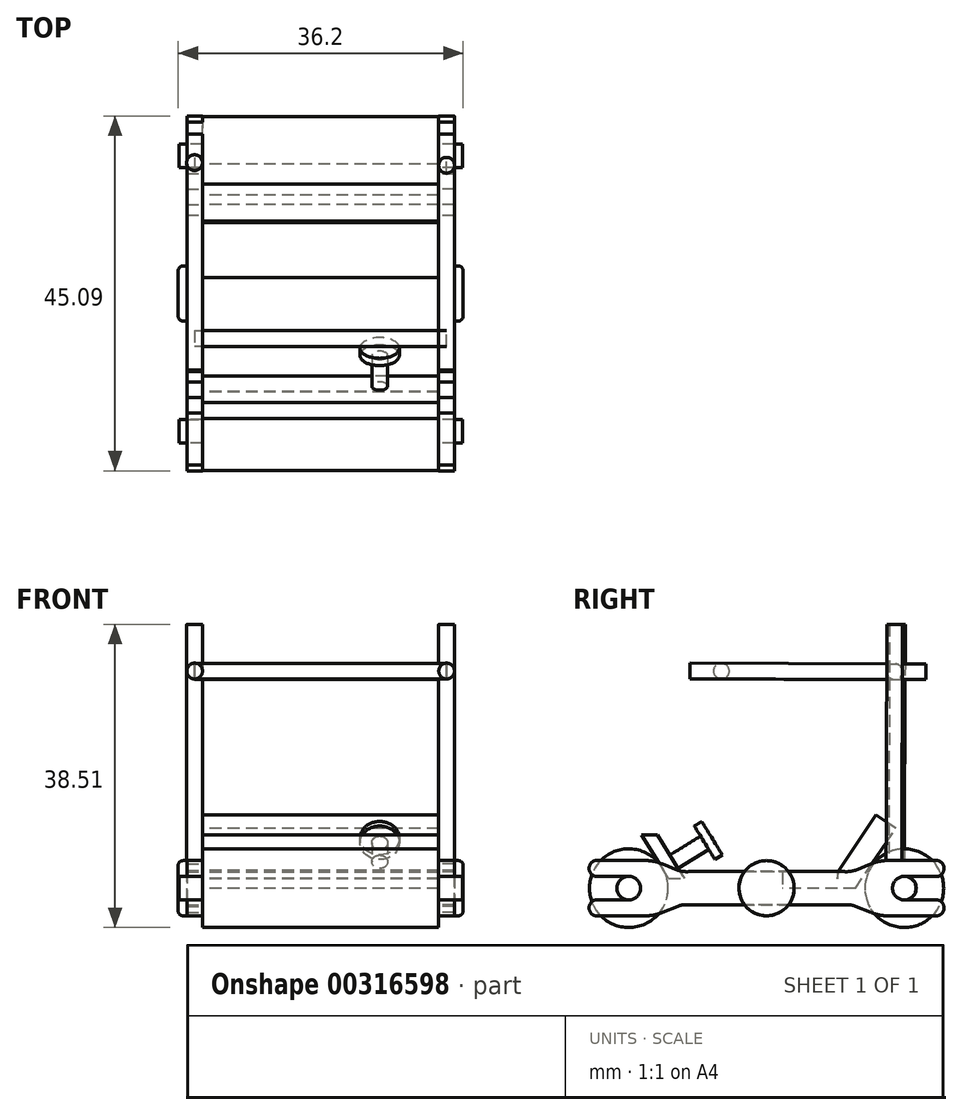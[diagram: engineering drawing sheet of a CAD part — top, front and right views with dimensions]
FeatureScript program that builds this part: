
annotation { "Feature Type Name" : "Feature", "Feature Type Description" : "" }
export const myFeature = defineFeature(function(context is Context, id is Id, definition is map)
    precondition{}
    {
        {
            var Q0;
            Q0=qCreatedBy(makeId("Right.planeOp"),FACE);
            var sketch = newSketch(context, id + "F0", { "sketchPlane" : qUnion([Q0])});
            skCircle(sketch, "E0", {"center": v(0, 0) * mm, "radius": 5 * mm});
            skCircle(sketch, "E1", {"center": v(-35, 0) * mm, "radius": 5 * mm});
            skSolve(sketch);
        }
        {
            var Q0;
            Q0 = qSketchRegion(id + "F0", true);
            extrude(context, id + "F1", {"entities" : qUnion([Q0]), "depth" : 30 * mm});
        }
        {
            var Q0;
            Q0=makeQuery(id+"F1.opExtrude","CAP_FACE",FACE,{"disambiguationData":[OSD([sQuery(id+"F0.wireOp",EDGE,"E0")])],"isStart":false});
            var sketch = newSketch(context, id + "F2", { "sketchPlane" : qUnion([Q0])});
            skCircle(sketch, "E2", {"center": v(0, 0) * mm, "radius": 1.5 * mm});
            skCircle(sketch, "E3", {"center": v(-35, 0) * mm, "radius": 1.5 * mm});
            skSolve(sketch);
        }
        {
            var Q0;
            Q0 = qSketchRegion(id + "F2", true);
            extrude(context, id + "F3", {"entities" : qUnion([Q0]), "operationType" : NewBodyOperationType.ADD, "depth" : 3 * mm, "hasSecondDirection" : true, "secondDirectionOppositeDirection" : true, "secondDirectionDepth" : 33 * mm});
        }
        {
            var Q0;
            Q0=makeQuery(id+"F1.opExtrude","CAP_FACE",FACE,{"disambiguationData":[OSD([sQuery(id+"F0.wireOp",EDGE,"E0")])],"isStart":false});
            var sketch = newSketch(context, id + "F4", { "sketchPlane" : qUnion([Q0])});
            skLineSegment(sketch, "E4", {"start": v(-35, 3.5) * mm, "end": v(-39.28, 3.5) * mm});
            skPoint(sketch, "E5.orphan", {"position": v(-45, -3.5) * mm});
            skLineSegment(sketch, "E6", {"start": v(-35, 1.5) * mm, "end": v(-39.28, 1.5) * mm});
            skArc(sketch, "E7", {"start": v(-33.5, 0) * mm, "mid": v(-33.94, 1.06) * mm, "end": v(-35, 1.5) * mm});
            skLineSegment(sketch, "E8", {"start": v(-30.73, 3.07) * mm, "end": v(-28.77, 2.29) * mm});
            skArc(sketch, "E9", {"start": v(-30.73, 3.07) * mm, "mid": v(-31.7, 3.38) * mm, "end": v(-32.7, 3.5) * mm});
            skLineSegment(sketch, "E10.trimOffspring", {"start": v(-32.7, 3.5) * mm, "end": v(-35, 3.5) * mm});
            skArc(sketch, "E11", {"start": v(-39.28, 3.5) * mm, "mid": v(-40.04, 2.5) * mm, "end": v(-39.28, 1.5) * mm});
            skPoint(sketch, "E12.start.orphan", {"position": v(-40, 2.5) * mm});
            skPoint(sketch, "E13.orphan", {"position": v(-40, 3.5) * mm});
            skPoint(sketch, "E14.orphan", {"position": v(-40, 1.5) * mm});
            skLineSegment(sketch, "E15", {"start": v(5, 11.22) * mm, "end": v(-17.5, 11.22) * mm, "construction": true});
            skLineSegment(sketch, "E16", {"start": v(-17.5, 11.22) * mm, "end": v(-17.5, -11.24) * mm, "construction": true});
            skArc(sketch, "E17", {"start": v(-28.77, 2.29) * mm, "mid": v(-28.1, 2.13) * mm, "end": v(-27.42, 2.1) * mm});
            skPoint(sketch, "E18.orphan", {"position": v(-28.31, 2.1) * mm});
            skLineSegment(sketch, "E19.trimOffspring", {"start": v(-27.42, 2.1) * mm, "end": v(-17.5, 2.1) * mm});
            skLineSegment(sketch, "E20", {"start": v(-53.45, 0) * mm, "end": v(6.7, 0) * mm, "construction": true});
            skLineSegment(sketch, "E21.MirrorCS", {"start": v(-7.58, 2.1) * mm, "end": v(-17.5, 2.1) * mm});
            skArc(sketch, "E22.MirrorCS", {"start": v(4.28, 3.5) * mm, "mid": v(5.04, 2.5) * mm, "end": v(4.28, 1.5) * mm});
            skArc(sketch, "E23.MirrorCS", {"start": v(-6.23, 2.29) * mm, "mid": v(-6.9, 2.13) * mm, "end": v(-7.58, 2.1) * mm});
            skLineSegment(sketch, "E24.MirrorCS", {"start": v(0, 3.5) * mm, "end": v(4.28, 3.5) * mm});
            skPoint(sketch, "E25.MirrorP", {"position": v(-6.69, 2.1) * mm});
            skLineSegment(sketch, "E26.MirrorCS", {"start": v(0, 1.5) * mm, "end": v(4.28, 1.5) * mm});
            skArc(sketch, "E27.MirrorCS", {"start": v(-1.5, 0) * mm, "mid": v(-1.06, 1.06) * mm, "end": v(0, 1.5) * mm});
            skPoint(sketch, "E28.MirrorP", {"position": v(5, 1.5) * mm});
            skLineSegment(sketch, "E29.MirrorCS", {"start": v(-2.3, 3.5) * mm, "end": v(0, 3.5) * mm});
            skLineSegment(sketch, "E30.MirrorCS", {"start": v(-4.27, 3.07) * mm, "end": v(-6.23, 2.29) * mm});
            skArc(sketch, "E31.MirrorCS", {"start": v(-4.27, 3.07) * mm, "mid": v(-3.3, 3.38) * mm, "end": v(-2.3, 3.5) * mm});
            skPoint(sketch, "E32.MirrorP", {"position": v(5, 2.5) * mm});
            skPoint(sketch, "E33.MirrorP", {"position": v(5, 3.5) * mm});
            skArc(sketch, "E34.MirrorCS", {"start": v(-6.23, -2.29) * mm, "mid": v(-6.9, -2.13) * mm, "end": v(-7.58, -2.1) * mm});
            skArc(sketch, "E35.MirrorCS", {"start": v(-4.27, -3.07) * mm, "mid": v(-3.3, -3.38) * mm, "end": v(-2.3, -3.5) * mm});
            skLineSegment(sketch, "E36.MirrorCS", {"start": v(-4.27, -3.07) * mm, "end": v(-6.23, -2.29) * mm});
            skLineSegment(sketch, "E37.MirrorCS", {"start": v(-2.3, -3.5) * mm, "end": v(0, -3.5) * mm});
            skLineSegment(sketch, "E38.MirrorCS", {"start": v(-30.73, -3.07) * mm, "end": v(-28.77, -2.29) * mm});
            skArc(sketch, "E39.MirrorCS", {"start": v(4.28, -3.5) * mm, "mid": v(5.04, -2.5) * mm, "end": v(4.28, -1.5) * mm});
            skArc(sketch, "E40.MirrorCS", {"start": v(-30.73, -3.07) * mm, "mid": v(-31.7, -3.38) * mm, "end": v(-32.7, -3.5) * mm});
            skArc(sketch, "E41.MirrorCS", {"start": v(-39.28, -3.5) * mm, "mid": v(-40.04, -2.5) * mm, "end": v(-39.28, -1.5) * mm});
            skLineSegment(sketch, "E42.MirrorCS", {"start": v(-32.7, -3.5) * mm, "end": v(-35, -3.5) * mm});
            skArc(sketch, "E43.MirrorCS", {"start": v(-28.77, -2.29) * mm, "mid": v(-28.1, -2.13) * mm, "end": v(-27.42, -2.1) * mm});
            skArc(sketch, "E44.MirrorCS", {"start": v(-1.5, 0) * mm, "mid": v(-1.06, -1.06) * mm, "end": v(0, -1.5) * mm});
            skArc(sketch, "E45.MirrorCS", {"start": v(-33.5, 0) * mm, "mid": v(-33.94, -1.06) * mm, "end": v(-35, -1.5) * mm});
            skLineSegment(sketch, "E46.MirrorCS", {"start": v(-7.58, -2.1) * mm, "end": v(-17.5, -2.1) * mm});
            skLineSegment(sketch, "E47.MirrorCS", {"start": v(0, -3.5) * mm, "end": v(4.28, -3.5) * mm});
            skLineSegment(sketch, "E48.MirrorCS", {"start": v(-35, -3.5) * mm, "end": v(-39.28, -3.5) * mm});
            skPoint(sketch, "E49.MirrorP", {"position": v(5, -3.5) * mm});
            skLineSegment(sketch, "E50.MirrorCS", {"start": v(0, -1.5) * mm, "end": v(4.28, -1.5) * mm});
            skPoint(sketch, "E51.MirrorP", {"position": v(-45, 3.5) * mm});
            skPoint(sketch, "E52.MirrorP", {"position": v(5, -1.5) * mm});
            skPoint(sketch, "E53.MirrorP", {"position": v(-40, -3.5) * mm});
            skPoint(sketch, "E54.MirrorP", {"position": v(5, -2.5) * mm});
            skPoint(sketch, "E55.MirrorP", {"position": v(-28.31, -2.1) * mm});
            skPoint(sketch, "E56.MirrorP", {"position": v(-40, -1.5) * mm});
            skLineSegment(sketch, "E57.MirrorCS", {"start": v(-35, -1.5) * mm, "end": v(-39.28, -1.5) * mm});
            skPoint(sketch, "E58.MirrorP", {"position": v(-6.69, -2.1) * mm});
            skPoint(sketch, "E59.MirrorP", {"position": v(-40, -2.5) * mm});
            skLineSegment(sketch, "E60.MirrorCS", {"start": v(-27.42, -2.1) * mm, "end": v(-17.5, -2.1) * mm});
            skSolve(sketch);
        }
        {
            var Q0;
            Q0 = qSketchRegion(id + "F4", true);
            extrude(context, id + "F5", {"entities" : qUnion([Q0]), "depth" : 2 * mm});
        }
        {
            var Q0;
            Q0=makeQuery(id+"F1.opExtrude","CAP_FACE",FACE,{"disambiguationData":[OSD([sQuery(id+"F0.wireOp",EDGE,"E0")])],"isStart":true});
            var sketch = newSketch(context, id + "F6", { "sketchPlane" : qUnion([Q0])});
            skPoint(sketch, "E61.orphan", {"position": v(6.62, -3.1) * mm});
            skLineSegment(sketch, "E62", {"start": v(-0.01, 3.5) * mm, "end": v(-4.3, 3.5) * mm});
            skPoint(sketch, "E63.orphan", {"position": v(-26.63, -3.7) * mm});
            skLineSegment(sketch, "E64", {"start": v(-0.01, 1.5) * mm, "end": v(-4.3, 1.5) * mm});
            skArc(sketch, "E65", {"start": v(1.49, 0) * mm, "mid": v(1.05, 1.06) * mm, "end": v(-0.01, 1.5) * mm});
            skLineSegment(sketch, "E66", {"start": v(4.26, 3.07) * mm, "end": v(6.21, 2.29) * mm});
            skArc(sketch, "E67", {"start": v(4.26, 3.07) * mm, "mid": v(3.3, 3.38) * mm, "end": v(2.3, 3.5) * mm});
            skLineSegment(sketch, "E68.trimOffspring", {"start": v(2.3, 3.5) * mm, "end": v(-0.01, 3.5) * mm});
            skArc(sketch, "E69", {"start": v(-4.3, 3.5) * mm, "mid": v(-5.05, 2.5) * mm, "end": v(-4.3, 1.5) * mm});
            skPoint(sketch, "E70.start.orphan", {"position": v(-5.01, 2.5) * mm});
            skPoint(sketch, "E71.orphan", {"position": v(-5.01, 3.5) * mm});
            skPoint(sketch, "E72.orphan", {"position": v(-5.01, 1.5) * mm});
            skLineSegment(sketch, "E73", {"start": v(39.99, 11.03) * mm, "end": v(17.49, 11.03) * mm, "construction": true});
            skLineSegment(sketch, "E74", {"start": v(17.49, 11.22) * mm, "end": v(17.49, -11.24) * mm, "construction": true});
            skArc(sketch, "E75", {"start": v(6.21, 2.29) * mm, "mid": v(6.88, 2.13) * mm, "end": v(7.57, 2.1) * mm});
            skPoint(sketch, "E76.orphan", {"position": v(6.67, 2.1) * mm});
            skLineSegment(sketch, "E77.trimOffspring", {"start": v(7.57, 2.1) * mm, "end": v(17.49, 2.1) * mm});
            skLineSegment(sketch, "E78", {"start": v(-18.46, 0) * mm, "end": v(41.68, 0) * mm, "construction": true});
            skLineSegment(sketch, "E79.MirrorCS", {"start": v(27.4, 2.1) * mm, "end": v(17.49, 2.1) * mm});
            skArc(sketch, "E80.MirrorCS", {"start": v(39.27, 3.5) * mm, "mid": v(40.03, 2.5) * mm, "end": v(39.27, 1.5) * mm});
            skArc(sketch, "E81.MirrorCS", {"start": v(28.76, 2.29) * mm, "mid": v(28.1, 2.13) * mm, "end": v(27.4, 2.1) * mm});
            skLineSegment(sketch, "E82.MirrorCS", {"start": v(34.99, 3.5) * mm, "end": v(39.27, 3.5) * mm});
            skPoint(sketch, "E83.MirrorP", {"position": v(28.3, 2.1) * mm});
            skLineSegment(sketch, "E84.MirrorCS", {"start": v(34.99, 1.5) * mm, "end": v(39.27, 1.5) * mm});
            skArc(sketch, "E85.MirrorCS", {"start": v(33.49, 0) * mm, "mid": v(33.93, 1.06) * mm, "end": v(34.99, 1.5) * mm});
            skPoint(sketch, "E86.MirrorP", {"position": v(39.99, 1.5) * mm});
            skLineSegment(sketch, "E87.MirrorCS", {"start": v(32.68, 3.5) * mm, "end": v(34.99, 3.5) * mm});
            skLineSegment(sketch, "E88.MirrorCS", {"start": v(30.72, 3.07) * mm, "end": v(28.76, 2.29) * mm});
            skArc(sketch, "E89.MirrorCS", {"start": v(30.72, 3.07) * mm, "mid": v(31.68, 3.38) * mm, "end": v(32.68, 3.5) * mm});
            skPoint(sketch, "E90.MirrorP", {"position": v(39.99, 2.5) * mm});
            skPoint(sketch, "E91.MirrorP", {"position": v(39.99, 3.5) * mm});
            skArc(sketch, "E92.MirrorCS", {"start": v(28.76, -2.29) * mm, "mid": v(28.1, -2.13) * mm, "end": v(27.4, -2.1) * mm});
            skArc(sketch, "E93.MirrorCS", {"start": v(30.72, -3.07) * mm, "mid": v(31.68, -3.38) * mm, "end": v(32.68, -3.5) * mm});
            skLineSegment(sketch, "E94.MirrorCS", {"start": v(30.72, -3.07) * mm, "end": v(28.76, -2.29) * mm});
            skLineSegment(sketch, "E95.MirrorCS", {"start": v(32.68, -3.5) * mm, "end": v(34.99, -3.5) * mm});
            skLineSegment(sketch, "E96.MirrorCS", {"start": v(4.26, -3.07) * mm, "end": v(6.21, -2.29) * mm});
            skArc(sketch, "E97.MirrorCS", {"start": v(39.27, -3.5) * mm, "mid": v(40.03, -2.5) * mm, "end": v(39.27, -1.5) * mm});
            skArc(sketch, "E98.MirrorCS", {"start": v(4.26, -3.07) * mm, "mid": v(3.3, -3.38) * mm, "end": v(2.3, -3.5) * mm});
            skArc(sketch, "E99.MirrorCS", {"start": v(-4.3, -3.5) * mm, "mid": v(-5.05, -2.5) * mm, "end": v(-4.3, -1.5) * mm});
            skLineSegment(sketch, "E100.MirrorCS", {"start": v(2.3, -3.5) * mm, "end": v(-0.01, -3.5) * mm});
            skArc(sketch, "E101.MirrorCS", {"start": v(6.21, -2.29) * mm, "mid": v(6.88, -2.13) * mm, "end": v(7.57, -2.1) * mm});
            skArc(sketch, "E102.MirrorCS", {"start": v(33.49, 0) * mm, "mid": v(33.93, -1.06) * mm, "end": v(34.99, -1.5) * mm});
            skArc(sketch, "E103.MirrorCS", {"start": v(1.49, 0) * mm, "mid": v(1.05, -1.06) * mm, "end": v(-0.01, -1.5) * mm});
            skLineSegment(sketch, "E104.MirrorCS", {"start": v(27.4, -2.1) * mm, "end": v(17.49, -2.1) * mm});
            skLineSegment(sketch, "E105.MirrorCS", {"start": v(34.99, -3.5) * mm, "end": v(39.27, -3.5) * mm});
            skLineSegment(sketch, "E106.MirrorCS", {"start": v(-0.01, -3.5) * mm, "end": v(-4.3, -3.5) * mm});
            skPoint(sketch, "E107.MirrorP", {"position": v(39.99, -3.5) * mm});
            skLineSegment(sketch, "E108.MirrorCS", {"start": v(34.99, -1.5) * mm, "end": v(39.27, -1.5) * mm});
            skPoint(sketch, "E109.MirrorP", {"position": v(-26.63, 3.3) * mm});
            skPoint(sketch, "E110.MirrorP", {"position": v(39.99, -1.5) * mm});
            skPoint(sketch, "E111.MirrorP", {"position": v(-5.01, -3.5) * mm});
            skPoint(sketch, "E112.MirrorP", {"position": v(39.99, -2.5) * mm});
            skPoint(sketch, "E113.MirrorP", {"position": v(6.67, -2.1) * mm});
            skPoint(sketch, "E114.MirrorP", {"position": v(-5.01, -1.5) * mm});
            skLineSegment(sketch, "E115.MirrorCS", {"start": v(-0.01, -1.5) * mm, "end": v(-4.3, -1.5) * mm});
            skPoint(sketch, "E116.MirrorP", {"position": v(28.3, -2.1) * mm});
            skPoint(sketch, "E117.MirrorP", {"position": v(-5.01, -2.5) * mm});
            skLineSegment(sketch, "E118.MirrorCS", {"start": v(7.57, -2.1) * mm, "end": v(17.49, -2.1) * mm});
            skSolve(sketch);
        }
        {
            var Q0;
            Q0 = qSketchRegion(id + "F6", true);
            extrude(context, id + "F7", {"entities" : qUnion([Q0]), "depth" : 2 * mm});
        }
        {
            var Q0;
            Q0=makeQuery(id+"F5.opExtrude","CAP_FACE",FACE,{"disambiguationData":[OSD([sQuery(id+"F4.wireOp",EDGE,"E4"),sQuery(id+"F4.wireOp",EDGE,"E6"),sQuery(id+"F4.wireOp",EDGE,"E7"),sQuery(id+"F4.wireOp",EDGE,"E8"),sQuery(id+"F4.wireOp",EDGE,"E9"),sQuery(id+"F4.wireOp",EDGE,"E10.trimOffspring"),sQuery(id+"F4.wireOp",EDGE,"E11"),sQuery(id+"F4.wireOp",EDGE,"E17"),sQuery(id+"F4.wireOp",EDGE,"E19.trimOffspring"),sQuery(id+"F4.wireOp",EDGE,"E21.MirrorCS"),sQuery(id+"F4.wireOp",EDGE,"E22.MirrorCS"),sQuery(id+"F4.wireOp",EDGE,"E23.MirrorCS"),sQuery(id+"F4.wireOp",EDGE,"E24.MirrorCS"),sQuery(id+"F4.wireOp",EDGE,"E26.MirrorCS"),sQuery(id+"F4.wireOp",EDGE,"E27.MirrorCS"),sQuery(id+"F4.wireOp",EDGE,"E29.MirrorCS"),sQuery(id+"F4.wireOp",EDGE,"E30.MirrorCS"),sQuery(id+"F4.wireOp",EDGE,"E31.MirrorCS"),sQuery(id+"F4.wireOp",EDGE,"E34.MirrorCS"),sQuery(id+"F4.wireOp",EDGE,"E35.MirrorCS"),sQuery(id+"F4.wireOp",EDGE,"E36.MirrorCS"),sQuery(id+"F4.wireOp",EDGE,"E37.MirrorCS"),sQuery(id+"F4.wireOp",EDGE,"E38.MirrorCS"),sQuery(id+"F4.wireOp",EDGE,"E39.MirrorCS"),sQuery(id+"F4.wireOp",EDGE,"E40.MirrorCS"),sQuery(id+"F4.wireOp",EDGE,"E41.MirrorCS"),sQuery(id+"F4.wireOp",EDGE,"E42.MirrorCS"),sQuery(id+"F4.wireOp",EDGE,"E43.MirrorCS"),sQuery(id+"F4.wireOp",EDGE,"E44.MirrorCS"),sQuery(id+"F4.wireOp",EDGE,"E45.MirrorCS"),sQuery(id+"F4.wireOp",EDGE,"E46.MirrorCS"),sQuery(id+"F4.wireOp",EDGE,"E47.MirrorCS"),sQuery(id+"F4.wireOp",EDGE,"E48.MirrorCS"),sQuery(id+"F4.wireOp",EDGE,"E50.MirrorCS"),sQuery(id+"F4.wireOp",EDGE,"E57.MirrorCS"),sQuery(id+"F4.wireOp",EDGE,"E60.MirrorCS")])],"isStart":false});
            var sketch = newSketch(context, id + "F8", { "sketchPlane" : qUnion([Q0])});
            skLineSegment(sketch, "E119", {"start": v(0, 9.77) * mm, "end": v(-17.5, 9.77) * mm, "construction": true});
            skLineSegment(sketch, "E120", {"start": v(-17.5, 9.77) * mm, "end": v(-17.5, -15.8) * mm, "construction": true});
            skLineSegment(sketch, "E121", {"start": v(-41.77, 0) * mm, "end": v(7.9, 0) * mm, "construction": true});
            skCircle(sketch, "E122", {"center": v(-17.5, 0) * mm, "radius": 3.5 * mm});
            skSolve(sketch);
        }
        {
            var Q0;
            Q0 = qSketchRegion(id + "F8", true);
            extrude(context, id + "F9", {"entities" : qUnion([Q0]), "operationType" : NewBodyOperationType.ADD, "depth" : 1.1 * mm});
        }
        {
            var Q0;
            Q0=makeQuery(id+"F9.opExtrude","CAP_EDGE",EDGE,{"disambiguationData":[OSD([sQuery(id+"F8.wireOp",EDGE,"E122")])],"isStart":false});
            fillet(context, id + "F10", {"entities" : qUnion([Q0]), "radius" : 0.6 * mm, "tangentPropagation" : true, "allowEdgeOverflow" : false});
        }
        {
            var Q0;
            Q0=makeQuery(id+"F5.opExtrude","SWEPT_FACE",FACE,{"disambiguationData":[OSD([sQuery(id+"F4.wireOp",EDGE,"E29.MirrorCS")])]});
            var sketch = newSketch(context, id + "F11", { "sketchPlane" : qUnion([Q0])});
            skLineSegment(sketch, "E123.bottom", {"start": v(30, -2.32) * mm, "end": v(32, -2.32) * mm});
            skLineSegment(sketch, "E123.top", {"start": v(30, -0.32) * mm, "end": v(32, -0.32) * mm});
            skLineSegment(sketch, "E123.left", {"start": v(30, -2.32) * mm, "end": v(30, -0.32) * mm});
            skLineSegment(sketch, "E123.right", {"start": v(32, -2.32) * mm, "end": v(32, -0.32) * mm});
            skPoint(sketch, "E124.orphan", {"position": v(0, 0) * mm});
            skLineSegment(sketch, "E125.MirrorCS", {"start": v(-0.04, -2) * mm, "end": v(-2.04, -1.96) * mm});
            skLineSegment(sketch, "E126.MirrorCS", {"start": v(-2.04, -1.96) * mm, "end": v(-2, 0.04) * mm});
            skLineSegment(sketch, "E127.MirrorCS", {"start": v(0, 0) * mm, "end": v(-2, 0.04) * mm});
            skLineSegment(sketch, "E128.MirrorCS", {"start": v(-0.04, -2) * mm, "end": v(0, 0) * mm});
            skSolve(sketch);
        }
        {
            var Q0;
            Q0 = qSketchRegion(id + "F11", true);
            extrude(context, id + "F12", {"entities" : qUnion([Q0]), "depth" : 30 * mm});
        }
        {
            var Q0;
            Q0=makeQuery(id+"F12.opExtrude","SWEPT_FACE",FACE,{"disambiguationData":[OSD([sQuery(id+"F11.wireOp",EDGE,"E123.bottom")])]});
            var sketch = newSketch(context, id + "F13", { "sketchPlane" : qUnion([Q0])});
            skLineSegment(sketch, "E129.bottom", {"start": v(30, 28.5) * mm, "end": v(32, 28.5) * mm});
            skLineSegment(sketch, "E129.top", {"start": v(30, 26.5) * mm, "end": v(32, 26.5) * mm});
            skLineSegment(sketch, "E129.left", {"start": v(30, 28.5) * mm, "end": v(30, 26.5) * mm});
            skLineSegment(sketch, "E129.right", {"start": v(32, 28.5) * mm, "end": v(32, 26.5) * mm});
            skLineSegment(sketch, "E130.MirrorCS", {"start": v(-2, 28.5) * mm, "end": v(-2, 26.5) * mm});
            skLineSegment(sketch, "E131.MirrorCS", {"start": v(0, 28.5) * mm, "end": v(0, 26.5) * mm});
            skLineSegment(sketch, "E132.MirrorCS", {"start": v(0, 26.5) * mm, "end": v(-2, 26.5) * mm});
            skLineSegment(sketch, "E133.MirrorCS", {"start": v(0, 28.5) * mm, "end": v(-2, 28.5) * mm});
            skPoint(sketch, "E134.MirrorCS.start.orphan", {"position": v(0, 33.5) * mm});
            skPoint(sketch, "E135.start.orphan", {"position": v(30, 33.5) * mm});
            skSolve(sketch);
        }
        {
            var Q0;
            Q0 = qSketchRegion(id + "F13", true);
            extrude(context, id + "F14", {"entities" : qUnion([Q0]), "depth" : 25 * mm, "hasSecondDirection" : true, "secondDirectionOppositeDirection" : true, "secondDirectionDepth" : 5 * mm});
        }
        {
            var Q0;
            Q0=makeQuery(id+"F14.opExtrude","SWEPT_FACE",FACE,{"disambiguationData":[OSD([sQuery(id+"F13.wireOp",EDGE,"E129.left")])]});
            var sketch = newSketch(context, id + "F15", { "sketchPlane" : qUnion([Q0])});
            skLineSegment(sketch, "E136.bottom", {"start": v(0.23, 28.5) * mm, "end": v(2.23, 28.5) * mm});
            skLineSegment(sketch, "E136.top", {"start": v(0.23, 26.5) * mm, "end": v(2.23, 26.5) * mm});
            skLineSegment(sketch, "E136.left", {"start": v(0.23, 28.5) * mm, "end": v(0.23, 26.5) * mm});
            skLineSegment(sketch, "E136.right", {"start": v(2.23, 28.5) * mm, "end": v(2.23, 26.5) * mm});
            skLineSegment(sketch, "E137", {"start": v(2.23, 28.5) * mm, "end": v(27.23, 28.59) * mm, "construction": true});
            skPoint(sketch, "E138", {"position": v(12.23, 28.54) * mm});
            skLineSegment(sketch, "E139", {"start": v(12.23, 28.54) * mm, "end": v(12.25, 22.13) * mm, "construction": true});
            skLineSegment(sketch, "E140.MirrorCS", {"start": v(22.23, 28.57) * mm, "end": v(22.24, 26.57) * mm});
            skLineSegment(sketch, "E141.MirrorCS", {"start": v(24.23, 28.58) * mm, "end": v(24.24, 26.58) * mm});
            skLineSegment(sketch, "E142.MirrorCS", {"start": v(24.23, 28.58) * mm, "end": v(22.23, 28.57) * mm});
            skLineSegment(sketch, "E143.MirrorCS", {"start": v(24.24, 26.58) * mm, "end": v(22.24, 26.57) * mm});
            skSolve(sketch);
        }
        {
            var Q0;
            Q0 = qSketchRegion(id + "F15", true);
            extrude(context, id + "F16", {"entities" : qUnion([Q0]), "depth" : 31 * mm, "hasSecondDirection" : true, "secondDirectionOppositeDirection" : true, "secondDirectionDepth" : 1 * mm});
        }
        {
            var Q0;
            Q0=makeQuery(id+"F7.opExtrude","CAP_FACE",FACE,{"disambiguationData":[OSD([sQuery(id+"F6.wireOp",EDGE,"E62"),sQuery(id+"F6.wireOp",EDGE,"E64"),sQuery(id+"F6.wireOp",EDGE,"E65"),sQuery(id+"F6.wireOp",EDGE,"E66"),sQuery(id+"F6.wireOp",EDGE,"E67"),sQuery(id+"F6.wireOp",EDGE,"E68.trimOffspring"),sQuery(id+"F6.wireOp",EDGE,"E69"),sQuery(id+"F6.wireOp",EDGE,"E75"),sQuery(id+"F6.wireOp",EDGE,"E77.trimOffspring"),sQuery(id+"F6.wireOp",EDGE,"E79.MirrorCS"),sQuery(id+"F6.wireOp",EDGE,"E80.MirrorCS"),sQuery(id+"F6.wireOp",EDGE,"E81.MirrorCS"),sQuery(id+"F6.wireOp",EDGE,"E82.MirrorCS"),sQuery(id+"F6.wireOp",EDGE,"E84.MirrorCS"),sQuery(id+"F6.wireOp",EDGE,"E85.MirrorCS"),sQuery(id+"F6.wireOp",EDGE,"E87.MirrorCS"),sQuery(id+"F6.wireOp",EDGE,"E88.MirrorCS"),sQuery(id+"F6.wireOp",EDGE,"E89.MirrorCS"),sQuery(id+"F6.wireOp",EDGE,"E92.MirrorCS"),sQuery(id+"F6.wireOp",EDGE,"E93.MirrorCS"),sQuery(id+"F6.wireOp",EDGE,"E94.MirrorCS"),sQuery(id+"F6.wireOp",EDGE,"E95.MirrorCS"),sQuery(id+"F6.wireOp",EDGE,"E96.MirrorCS"),sQuery(id+"F6.wireOp",EDGE,"E97.MirrorCS"),sQuery(id+"F6.wireOp",EDGE,"E98.MirrorCS"),sQuery(id+"F6.wireOp",EDGE,"E99.MirrorCS"),sQuery(id+"F6.wireOp",EDGE,"E100.MirrorCS"),sQuery(id+"F6.wireOp",EDGE,"E101.MirrorCS"),sQuery(id+"F6.wireOp",EDGE,"E102.MirrorCS"),sQuery(id+"F6.wireOp",EDGE,"E103.MirrorCS"),sQuery(id+"F6.wireOp",EDGE,"E104.MirrorCS"),sQuery(id+"F6.wireOp",EDGE,"E105.MirrorCS"),sQuery(id+"F6.wireOp",EDGE,"E106.MirrorCS"),sQuery(id+"F6.wireOp",EDGE,"E108.MirrorCS"),sQuery(id+"F6.wireOp",EDGE,"E115.MirrorCS"),sQuery(id+"F6.wireOp",EDGE,"E118.MirrorCS")])],"isStart":true});
            var sketch = newSketch(context, id + "F17", { "sketchPlane" : qUnion([Q0])});
            skLineSegment(sketch, "E144", {"start": v(-6.21, 0) * mm, "end": v(-1.09, 7.6) * mm});
            skLineSegment(sketch, "E145", {"start": v(-1.09, 7.6) * mm, "end": v(-3.58, 9.28) * mm});
            skLineSegment(sketch, "E146", {"start": v(-3.58, 9.28) * mm, "end": v(-8.33, 2.23) * mm});
            skPoint(sketch, "E147.oppositeSnap0", {"position": v(-17.49, 2.1) * mm});
            skLineSegment(sketch, "E147.bottom", {"start": v(-6.21, 0) * mm, "end": v(-15.46, 0) * mm});
            skLineSegment(sketch, "E147.top", {"start": v(-8.49, 2) * mm, "end": v(-15.46, 2) * mm});
            skLineSegment(sketch, "E148", {"start": v(-15.46, 2.1) * mm, "end": v(-15.46, 0) * mm});
            skPoint(sketch, "E149.orphan", {"position": v(-17.49, 2) * mm});
            skLineSegment(sketch, "E150", {"start": v(-8.49, 2) * mm, "end": v(-8.49, 1.16) * mm});
            skLineSegment(sketch, "E151", {"start": v(-8.49, 1.16) * mm, "end": v(-8.33, 2.23) * mm});
            skLineSegment(sketch, "E152.0", {"start": v(-29.96, 1.27) * mm, "end": v(-27.96, 1.22) * mm});
            skPoint(sketch, "E153.end.orphan", {"position": v(-28.08, 2.1) * mm});
            skLineSegment(sketch, "E154", {"start": v(-29.96, 1.27) * mm, "end": v(-33.37, 6.75) * mm});
            skLineSegment(sketch, "E155", {"start": v(-33.37, 6.75) * mm, "end": v(-31.37, 6.75) * mm});
            skLineSegment(sketch, "E156", {"start": v(-31.37, 6.75) * mm, "end": v(-27.96, 1.22) * mm});
            skSolve(sketch);
        }
        {
            var Q0;
            Q0 = qSketchRegion(id + "F17", true);
            extrude(context, id + "F18", {"entities" : qUnion([Q0]), "depth" : 30 * mm});
        }
        {
            var Q0;
            Q0=makeQuery(id+"F18.opExtrude","SWEPT_FACE",FACE,{"disambiguationData":[OSD([sQuery(id+"F17.wireOp",EDGE,"E156")])]});
            var sketch = newSketch(context, id + "F19", { "sketchPlane" : qUnion([Q0])});
            skLineSegment(sketch, "E157", {"start": v(-30, 22.23) * mm, "end": v(-15, 22.23) * mm, "construction": true});
            skPoint(sketch, "E158", {"position": v(-22.5, 22.23) * mm});
            skLineSegment(sketch, "E159", {"start": v(-22.5, 22.23) * mm, "end": v(-22.5, 18.23) * mm, "construction": true});
            skCircle(sketch, "E160", {"center": v(-22.5, 18.23) * mm, "radius": 1 * mm});
            skSolve(sketch);
        }
        {
            var Q0;
            Q0 = qSketchRegion(id + "F19", true);
            extrude(context, id + "F20", {"entities" : qUnion([Q0]), "operationType" : NewBodyOperationType.ADD, "depth" : 4.6 * mm});
        }
        {
            var Q0;
            Q0=makeQuery(id+"F20.opExtrude","CAP_FACE",FACE,{"disambiguationData":[OSD([sQuery(id+"F19.wireOp",EDGE,"E160")])],"isStart":false});
            var sketch = newSketch(context, id + "F21", { "sketchPlane" : qUnion([Q0])});
            skCircle(sketch, "E161", {"center": v(-22.5, 18.23) * mm, "radius": 2.5 * mm});
            skSolve(sketch);
        }
        {
            var Q0;
            Q0 = qSketchRegion(id + "F21", true);
            extrude(context, id + "F22", {"entities" : qUnion([Q0]), "operationType" : NewBodyOperationType.ADD, "depth" : 1.1 * mm});
        }
        {
            var Q0;
            Q0=makeQuery(id+"F12.opExtrude","SWEPT_EDGE",EDGE,{"disambiguationData":[OSD([sQuery(id+"F11.wireOp",EDGE,"E125.MirrorCS"),sQuery(id+"F11.wireOp",EDGE,"E126.MirrorCS")])]});
            var Q1;
            Q1=makeQuery(id+"F12.opExtrude","SWEPT_EDGE",EDGE,{"disambiguationData":[OSD([sQuery(id+"F11.wireOp",EDGE,"E126.MirrorCS"),sQuery(id+"F11.wireOp",EDGE,"E127.MirrorCS")])]});
            var Q2;
            Q2=makeQuery(id+"F12.opExtrude","SWEPT_EDGE",EDGE,{"disambiguationData":[OSD([sQuery(id+"F11.wireOp",EDGE,"E125.MirrorCS"),sQuery(id+"F11.wireOp",EDGE,"E128.MirrorCS")])]});
            var Q3;
            Q3=makeQuery(id+"F12.opExtrude","SWEPT_EDGE",EDGE,{"disambiguationData":[OSD([sQuery(id+"F11.wireOp",EDGE,"E127.MirrorCS"),sQuery(id+"F11.wireOp",EDGE,"E128.MirrorCS")])]});
            fillet(context, id + "F23", {"entities" : qUnion([Q0, Q1, Q2, Q3]), "radius" : 1 * mm, "tangentPropagation" : true, "allowEdgeOverflow" : false});
        }
        {
            var Q0;
            Q0=makeQuery(id+"F12.opExtrude","SWEPT_EDGE",EDGE,{"disambiguationData":[OSD([sQuery(id+"F4.wireOp",EDGE,"E29.MirrorCS"),sQuery(id+"F11.wireOp",EDGE,"E123.top"),sQuery(id+"F11.wireOp",EDGE,"E123.left")])]});
            var Q1;
            Q1=makeQuery(id+"F12.opExtrude","SWEPT_EDGE",EDGE,{"disambiguationData":[OSD([sQuery(id+"F11.wireOp",EDGE,"E123.bottom"),sQuery(id+"F11.wireOp",EDGE,"E123.right")])]});
            var Q2;
            Q2=makeQuery(id+"F12.opExtrude","SWEPT_EDGE",EDGE,{"disambiguationData":[OSD([sQuery(id+"F4.wireOp",EDGE,"E29.MirrorCS"),sQuery(id+"F11.wireOp",EDGE,"E123.top"),sQuery(id+"F11.wireOp",EDGE,"E123.right")])]});
            var Q3;
            Q3=makeQuery(id+"F12.opExtrude","SWEPT_EDGE",EDGE,{"disambiguationData":[OSD([sQuery(id+"F11.wireOp",EDGE,"E123.bottom"),sQuery(id+"F11.wireOp",EDGE,"E123.left")])]});
            fillet(context, id + "F24", {"entities" : qUnion([Q0, Q1, Q2, Q3]), "radius" : 1 * mm, "tangentPropagation" : true, "allowEdgeOverflow" : false});
        }
        {
            var Q0;
            Q0=makeQuery(id+"F14.opExtrude","SWEPT_EDGE",EDGE,{"disambiguationData":[OSD([sQuery(id+"F11.wireOp",EDGE,"E123.bottom"),sQuery(id+"F11.wireOp",EDGE,"E123.right"),sQuery(id+"F13.wireOp",EDGE,"E129.bottom"),sQuery(id+"F13.wireOp",EDGE,"E129.right")])]});
            var Q1;
            Q1=makeQuery(id+"F14.opExtrude","SWEPT_EDGE",EDGE,{"disambiguationData":[OSD([sQuery(id+"F11.wireOp",EDGE,"E123.bottom"),sQuery(id+"F11.wireOp",EDGE,"E123.right"),sQuery(id+"F13.wireOp",EDGE,"E129.top"),sQuery(id+"F13.wireOp",EDGE,"E129.right")])]});
            var Q2;
            Q2=makeQuery(id+"F14.opExtrude","SWEPT_EDGE",EDGE,{"disambiguationData":[OSD([sQuery(id+"F11.wireOp",EDGE,"E123.bottom"),sQuery(id+"F11.wireOp",EDGE,"E123.left"),sQuery(id+"F13.wireOp",EDGE,"E129.bottom"),sQuery(id+"F13.wireOp",EDGE,"E129.left")])]});
            var Q3;
            Q3=makeQuery(id+"F14.opExtrude","SWEPT_EDGE",EDGE,{"disambiguationData":[OSD([sQuery(id+"F11.wireOp",EDGE,"E123.bottom"),sQuery(id+"F11.wireOp",EDGE,"E123.left"),sQuery(id+"F13.wireOp",EDGE,"E129.top"),sQuery(id+"F13.wireOp",EDGE,"E129.left")])]});
            fillet(context, id + "F25", {"entities" : qUnion([Q0, Q1, Q2, Q3]), "radius" : 1 * mm, "tangentPropagation" : true, "allowEdgeOverflow" : false});
        }
        {
            var Q0;
            Q0=makeQuery(id+"F14.opExtrude","SWEPT_EDGE",EDGE,{"disambiguationData":[OSD([sQuery(id+"F13.wireOp",EDGE,"E130.MirrorCS"),sQuery(id+"F13.wireOp",EDGE,"E133.MirrorCS")])]});
            var Q1;
            Q1=makeQuery(id+"F14.opExtrude","SWEPT_EDGE",EDGE,{"disambiguationData":[OSD([sQuery(id+"F13.wireOp",EDGE,"E131.MirrorCS"),sQuery(id+"F13.wireOp",EDGE,"E133.MirrorCS")])]});
            var Q2;
            Q2=makeQuery(id+"F14.opExtrude","SWEPT_EDGE",EDGE,{"disambiguationData":[OSD([sQuery(id+"F13.wireOp",EDGE,"E130.MirrorCS"),sQuery(id+"F13.wireOp",EDGE,"E132.MirrorCS")])]});
            var Q3;
            Q3=makeQuery(id+"F14.opExtrude","SWEPT_EDGE",EDGE,{"disambiguationData":[OSD([sQuery(id+"F13.wireOp",EDGE,"E131.MirrorCS"),sQuery(id+"F13.wireOp",EDGE,"E132.MirrorCS")])]});
            fillet(context, id + "F26", {"entities" : qUnion([Q0, Q1, Q2, Q3]), "radius" : 1 * mm, "tangentPropagation" : true, "allowEdgeOverflow" : false});
        }
        {
            var Q0;
            Q0=makeQuery(id+"F16.opExtrude","SWEPT_EDGE",EDGE,{"disambiguationData":[OSD([sQuery(id+"F15.wireOp",EDGE,"E140.MirrorCS"),sQuery(id+"F15.wireOp",EDGE,"E142.MirrorCS")])]});
            var Q1;
            Q1=makeQuery(id+"F16.opExtrude","SWEPT_EDGE",EDGE,{"disambiguationData":[OSD([sQuery(id+"F11.wireOp",EDGE,"E123.bottom"),sQuery(id+"F11.wireOp",EDGE,"E123.left"),sQuery(id+"F13.wireOp",EDGE,"E129.bottom"),sQuery(id+"F13.wireOp",EDGE,"E129.left"),sQuery(id+"F15.wireOp",EDGE,"E141.MirrorCS"),sQuery(id+"F15.wireOp",EDGE,"E142.MirrorCS")])]});
            var Q2;
            Q2=makeQuery(id+"F16.opExtrude","SWEPT_EDGE",EDGE,{"disambiguationData":[OSD([sQuery(id+"F11.wireOp",EDGE,"E123.bottom"),sQuery(id+"F11.wireOp",EDGE,"E123.left"),sQuery(id+"F13.wireOp",EDGE,"E129.top"),sQuery(id+"F13.wireOp",EDGE,"E129.left"),sQuery(id+"F15.wireOp",EDGE,"E140.MirrorCS"),sQuery(id+"F15.wireOp",EDGE,"E143.MirrorCS")])]});
            var Q3;
            Q3=makeQuery(id+"F16.opExtrude","SWEPT_EDGE",EDGE,{"disambiguationData":[OSD([sQuery(id+"F15.wireOp",EDGE,"E141.MirrorCS"),sQuery(id+"F15.wireOp",EDGE,"E143.MirrorCS")])]});
            fillet(context, id + "F27", {"entities" : qUnion([Q0, Q1, Q2, Q3]), "radius" : 1 * mm, "tangentPropagation" : true, "allowEdgeOverflow" : false});
        }
        {
            var Q0;
            Q0=makeQuery(id+"F16.opExtrude","SWEPT_EDGE",EDGE,{"disambiguationData":[OSD([sQuery(id+"F11.wireOp",EDGE,"E123.bottom"),sQuery(id+"F11.wireOp",EDGE,"E123.left"),sQuery(id+"F13.wireOp",EDGE,"E129.bottom"),sQuery(id+"F13.wireOp",EDGE,"E129.left"),sQuery(id+"F15.wireOp",EDGE,"E136.bottom"),sQuery(id+"F15.wireOp",EDGE,"E136.left")])]});
            var Q1;
            Q1=makeQuery(id+"F16.opExtrude","SWEPT_EDGE",EDGE,{"disambiguationData":[OSD([sQuery(id+"F15.wireOp",EDGE,"E136.bottom"),sQuery(id+"F15.wireOp",EDGE,"E136.right")])]});
            var Q2;
            Q2=makeQuery(id+"F16.opExtrude","SWEPT_EDGE",EDGE,{"disambiguationData":[OSD([sQuery(id+"F15.wireOp",EDGE,"E136.top"),sQuery(id+"F15.wireOp",EDGE,"E136.left")])]});
            var Q3;
            Q3=makeQuery(id+"F16.opExtrude","SWEPT_EDGE",EDGE,{"disambiguationData":[OSD([sQuery(id+"F11.wireOp",EDGE,"E123.bottom"),sQuery(id+"F11.wireOp",EDGE,"E123.left"),sQuery(id+"F13.wireOp",EDGE,"E129.top"),sQuery(id+"F13.wireOp",EDGE,"E129.left"),sQuery(id+"F15.wireOp",EDGE,"E136.top"),sQuery(id+"F15.wireOp",EDGE,"E136.right")])]});
            fillet(context, id + "F28", {"entities" : qUnion([Q0, Q1, Q2, Q3]), "radius" : 1 * mm, "tangentPropagation" : true, "allowEdgeOverflow" : false});
        }
        {
            var Q0;
            Q0=makeQuery(id+"F7.opExtrude","CAP_FACE",FACE,{"disambiguationData":[OSD([sQuery(id+"F6.wireOp",EDGE,"E62"),sQuery(id+"F6.wireOp",EDGE,"E64"),sQuery(id+"F6.wireOp",EDGE,"E65"),sQuery(id+"F6.wireOp",EDGE,"E66"),sQuery(id+"F6.wireOp",EDGE,"E67"),sQuery(id+"F6.wireOp",EDGE,"E68.trimOffspring"),sQuery(id+"F6.wireOp",EDGE,"E69"),sQuery(id+"F6.wireOp",EDGE,"E75"),sQuery(id+"F6.wireOp",EDGE,"E77.trimOffspring"),sQuery(id+"F6.wireOp",EDGE,"E79.MirrorCS"),sQuery(id+"F6.wireOp",EDGE,"E80.MirrorCS"),sQuery(id+"F6.wireOp",EDGE,"E81.MirrorCS"),sQuery(id+"F6.wireOp",EDGE,"E82.MirrorCS"),sQuery(id+"F6.wireOp",EDGE,"E84.MirrorCS"),sQuery(id+"F6.wireOp",EDGE,"E85.MirrorCS"),sQuery(id+"F6.wireOp",EDGE,"E87.MirrorCS"),sQuery(id+"F6.wireOp",EDGE,"E88.MirrorCS"),sQuery(id+"F6.wireOp",EDGE,"E89.MirrorCS"),sQuery(id+"F6.wireOp",EDGE,"E92.MirrorCS"),sQuery(id+"F6.wireOp",EDGE,"E93.MirrorCS"),sQuery(id+"F6.wireOp",EDGE,"E94.MirrorCS"),sQuery(id+"F6.wireOp",EDGE,"E95.MirrorCS"),sQuery(id+"F6.wireOp",EDGE,"E96.MirrorCS"),sQuery(id+"F6.wireOp",EDGE,"E97.MirrorCS"),sQuery(id+"F6.wireOp",EDGE,"E98.MirrorCS"),sQuery(id+"F6.wireOp",EDGE,"E99.MirrorCS"),sQuery(id+"F6.wireOp",EDGE,"E100.MirrorCS"),sQuery(id+"F6.wireOp",EDGE,"E101.MirrorCS"),sQuery(id+"F6.wireOp",EDGE,"E102.MirrorCS"),sQuery(id+"F6.wireOp",EDGE,"E103.MirrorCS"),sQuery(id+"F6.wireOp",EDGE,"E104.MirrorCS"),sQuery(id+"F6.wireOp",EDGE,"E105.MirrorCS"),sQuery(id+"F6.wireOp",EDGE,"E106.MirrorCS"),sQuery(id+"F6.wireOp",EDGE,"E108.MirrorCS"),sQuery(id+"F6.wireOp",EDGE,"E115.MirrorCS"),sQuery(id+"F6.wireOp",EDGE,"E118.MirrorCS")])],"isStart":false});
            var sketch = newSketch(context, id + "F29", { "sketchPlane" : qUnion([Q0])});
            skLineSegment(sketch, "E162", {"start": v(0, 11.57) * mm, "end": v(17.5, 11.57) * mm, "construction": true});
            skLineSegment(sketch, "E163", {"start": v(17.5, 11.57) * mm, "end": v(17.5, -5.25) * mm, "construction": true});
            skCircle(sketch, "E164", {"center": v(17.5, 0) * mm, "radius": 3.5 * mm});
            skSolve(sketch);
        }
        {
            var Q0;
            Q0 = qSketchRegion(id + "F29", true);
            extrude(context, id + "F30", {"entities" : qUnion([Q0]), "operationType" : NewBodyOperationType.ADD, "depth" : 1.1 * mm});
        }
        {
            var Q0;
            Q0=makeQuery(id+"F30.opExtrude","CAP_FACE",FACE,{"disambiguationData":[OSD([sQuery(id+"F29.wireOp",EDGE,"E164")])],"isStart":false});
            fillet(context, id + "F31", {"entities" : qUnion([Q0]), "radius" : 0.6 * mm, "tangentPropagation" : true, "allowEdgeOverflow" : false});
        }
    });
